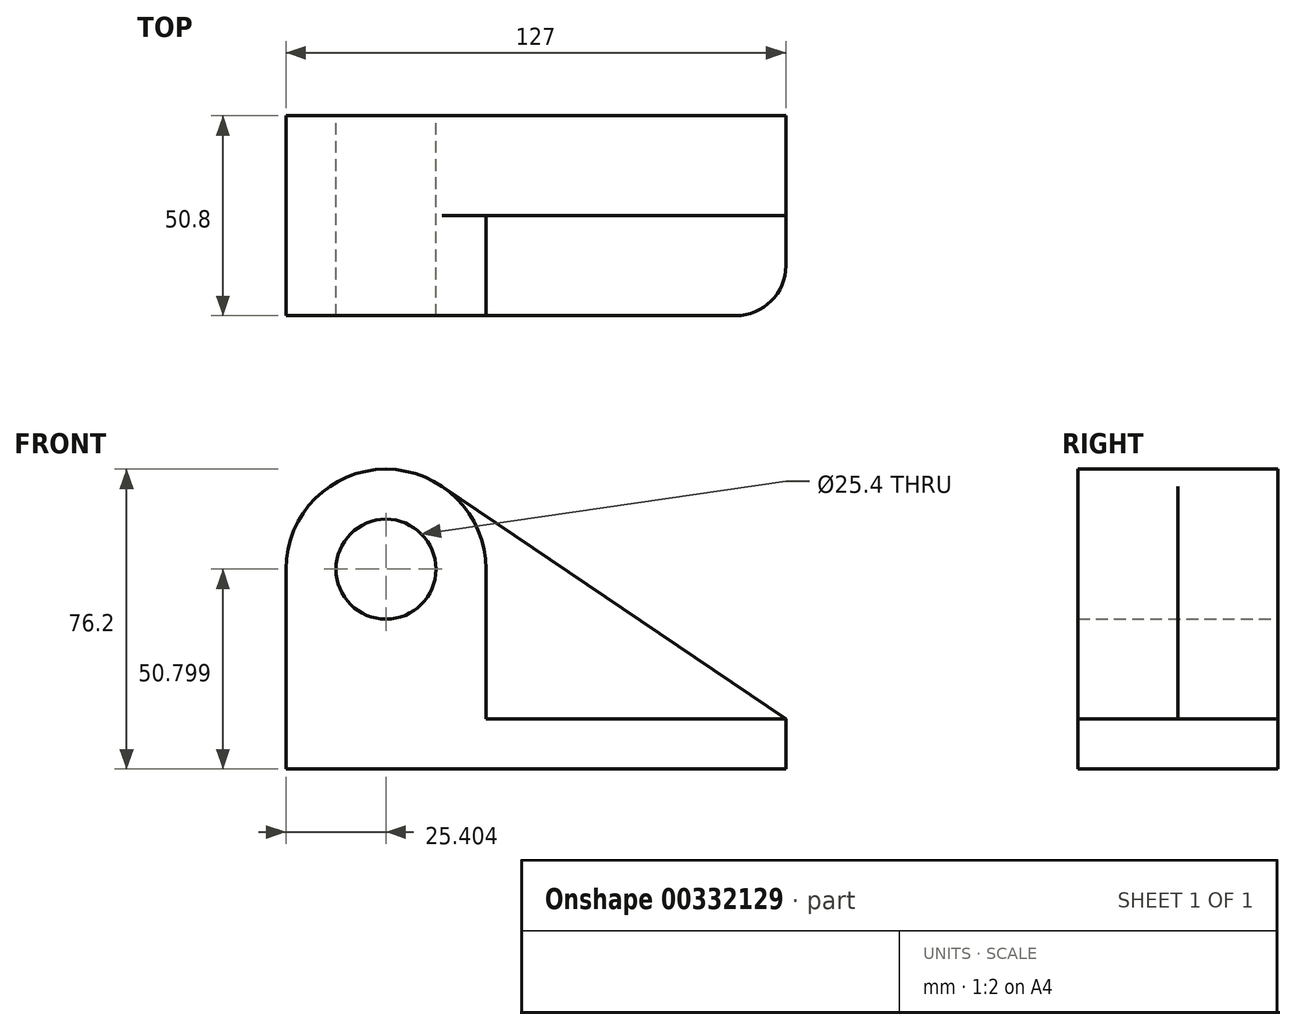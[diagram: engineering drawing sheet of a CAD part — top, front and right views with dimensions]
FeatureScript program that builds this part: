
annotation { "Feature Type Name" : "Feature", "Feature Type Description" : "" }
export const myFeature = defineFeature(function(context is Context, id is Id, definition is map)
    precondition{}
    {
        {
            var Q0;
            Q0=qCreatedBy(makeId("Front.planeOp"),FACE);
            var sketch = newSketch(context, id + "F0", { "sketchPlane" : qUnion([Q0])});
            skArc(sketch, "E0", {"start": v(-39.52, -10.12) * mm, "mid": v(-65.66, -8.71) * mm, "end": v(-79.16, -31.15) * mm});
            skCircle(sketch, "E1", {"center": v(-53.76, -31.15) * mm, "radius": 12.7 * mm});
            skLineSegment(sketch, "E2", {"start": v(-79.16, -31.15) * mm, "end": v(-79.16, -81.95) * mm});
            skLineSegment(sketch, "E3", {"start": v(-79.16, -81.95) * mm, "end": v(47.84, -81.95) * mm});
            skLineSegment(sketch, "E4", {"start": v(47.84, -81.95) * mm, "end": v(47.84, -69.25) * mm});
            skLineSegment(sketch, "E5", {"start": v(47.84, -69.25) * mm, "end": v(-39.52, -10.12) * mm});
            skSolve(sketch);
        }
        {
            var Q0;
            Q0=makeQuery(id+"F0.imprint","IMPRINT",FACE,{"disambiguationData":[TD([[makeQuery(id+"F0.imprint","IMPRINT",EDGE,{"derivedFrom":sQuery(id+"F0.wireOp",EDGE,"E0")}),1.0]])]});
            extrude(context, id + "F1", {"entities" : qUnion([Q0]), "depth" : 25.4 * mm});
        }
        {
            var Q0;
            Q0=makeQuery(id+"F1.opExtrude","CAP_FACE",FACE,{"disambiguationData":[OSD([sQuery(id+"F0.wireOp",EDGE,"E0"),sQuery(id+"F0.wireOp",EDGE,"E1"),sQuery(id+"F0.wireOp",EDGE,"E2"),sQuery(id+"F0.wireOp",EDGE,"E3"),sQuery(id+"F0.wireOp",EDGE,"E4"),sQuery(id+"F0.wireOp",EDGE,"E5")])],"isStart":false});
            var sketch = newSketch(context, id + "F2", { "sketchPlane" : qUnion([Q0])});
            skCircle(sketch, "E6", {"center": v(-53.76, -31.15) * mm, "radius": 12.7 * mm});
            skArc(sketch, "E7", {"start": v(-28.36, -31.15) * mm, "mid": v(-53.76, -5.75) * mm, "end": v(-79.16, -31.15) * mm});
            skLineSegment(sketch, "E8.bottom", {"start": v(47.84, -69.25) * mm, "end": v(47.84, -69.25) * mm});
            skLineSegment(sketch, "E8.top", {"start": v(47.84, -81.95) * mm, "end": v(47.84, -81.95) * mm});
            skLineSegment(sketch, "E8.left", {"start": v(47.84, -69.25) * mm, "end": v(47.84, -81.95) * mm});
            skLineSegment(sketch, "E8.right", {"start": v(47.84, -69.25) * mm, "end": v(47.84, -81.95) * mm});
            skLineSegment(sketch, "E9.bottom", {"start": v(-28.36, -69.25) * mm, "end": v(47.84, -69.25) * mm});
            skLineSegment(sketch, "E9.top", {"start": v(-79.16, -81.95) * mm, "end": v(47.84, -81.95) * mm});
            skLineSegment(sketch, "E9.left", {"start": v(-79.16, -69.25) * mm, "end": v(-79.16, -81.95) * mm});
            skLineSegment(sketch, "E10", {"start": v(-79.16, -31.15) * mm, "end": v(-79.16, -69.25) * mm});
            skLineSegment(sketch, "E11", {"start": v(-28.36, -31.15) * mm, "end": v(-28.36, -69.25) * mm});
            skSolve(sketch);
        }
        {
            var Q0;
            Q0=makeQuery(id+"F2.imprint","IMPRINT",FACE,{"disambiguationData":[TD([[makeQuery(id+"F2.imprint","IMPRINT",EDGE,{"derivedFrom":sQuery(id+"F2.wireOp",EDGE,"E6")}),-1.0]])]});
            extrude(context, id + "F3", {"entities" : qUnion([Q0]), "operationType" : NewBodyOperationType.ADD, "depth" : 25.4 * mm});
        }
        {
            var Q0;
            Q0=makeQuery(id+"F3.opExtrude","CAP_EDGE",EDGE,{"disambiguationData":[OSD([sQuery(id+"F2.wireOp",EDGE,"E8.left")])],"isStart":false});
            fillet(context, id + "F4", {"entities" : qUnion([Q0]), "radius" : 12.7 * mm, "tangentPropagation" : true, "allowEdgeOverflow" : false});
        }
    });
